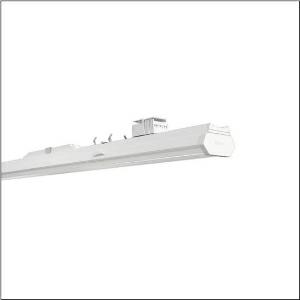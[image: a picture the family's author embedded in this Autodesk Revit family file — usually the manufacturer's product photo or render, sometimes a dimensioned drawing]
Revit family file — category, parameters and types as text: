
# Revit family: licross_r__11_protected_ho_51td13mn4gxs_7737
name_source: partatom
category: Lighting Fixtures
units: mm (PartAtom-declared; Revit-internal decimal feet)

## family parameters
Cut with Voids When Loaded = No
Host = Face
Light Source = No
Part Type = Normal
Room Calculation Point = No
Round Connector Dimension = Use Diameter
Shared = No

## types (1)
- --- (1 x LED, 16110 lm, 87.4 W, 4000K)
    Apparent Load = 87 VA
    CIE Flux Codes = 89 96 99 100 99
    Color Rendering = 80
    Color Temperature = 4000K
    Default Elevation = 1800 mm
    Description = Licross® 11 Protected HO, luminaire insert, of sheet steel, galvanised, coil coated, white, length: 1.500mm, width: 90mm, height: 101mm, LED rated luminous flux: 16.110lm, light colour: 840, control gear: ON/OFF Multilumen, with plug, 3-pole, with phase selection, mains connection: 220..240V, AC, 50/60Hz, rated input power: 87W, halogen-free wiring, primary light control with lens, of plastic, primary optical cover: cover, of PMMA, light emission: direct distribution, primary light characteristic: symmetric, protection rating (complete): IP54, insulation class (complete): insulation class I (protective earthing), certification: CE, ENEC, VDE, UKCA, protection symbol: D if used in an environment with non-conductive dust loads with corresponding accessories, impact resistance: IK06, permissible ambient temperature for indoor applications: -35..+35°C, corresponds to IFS (International Featured Standards) requirements for safety and quality in the food industry, reducing of maximum allowable ambient temperature of 5°C with ceiling mounting, LABS conformity tested according to VDMA 24364:2018-05, packaging unit: 1 piece
    Height = 92 mm
    Lamp = 1 x LED
    Lamp Light Flux = 16110 lm
    Lamp Power = 87.4 W
    Lamp count = 1
    Length = 1500 mm
    Luminous efficacy = 184 lm/W
    Manufacturer = Siteco
    ModVariant = No
    Model = 51TD13MN4GXS
    Mounting Place = Ceiling
    Mounting Type = Pendant
    Number of Poles = 1
    OnlyDefault = Yes
    Power Factor = 1
    Product Name = Licross® 11 Protected HO
    Product group = luminaire insert
    ProductGroupID = 902
    Protection Class = Protection class I
    Protection Degree = IP 54
    RLX_Detail_Level = 1
    RLX_Emergency_Light_Flux = 0 lm
    RLX_Emergency_Type = 0
    RLX_Emergency_Type_DB = No
    RlxData = <blob elided: 22025 chars, md5=0d22950a>
    Socket = socket
    Standby Power = 0 W
    System Light Flux = 16110 lm
    System Power = 87 W
    Type Comments = factory setting: luminous flux: 100 % | (A | C | E) | 203 mA
    Type Image = l_1256145.jpg
    URL = http://relux.com
    VarID = @adj_085724
    Voltage = 0 V
    Weight = 0.00 kg
    Width = 88 mm

## geometry (parser evidence)
native form markers: Blend x4, Sweep x11
no freeform markers — native parametric forms only
